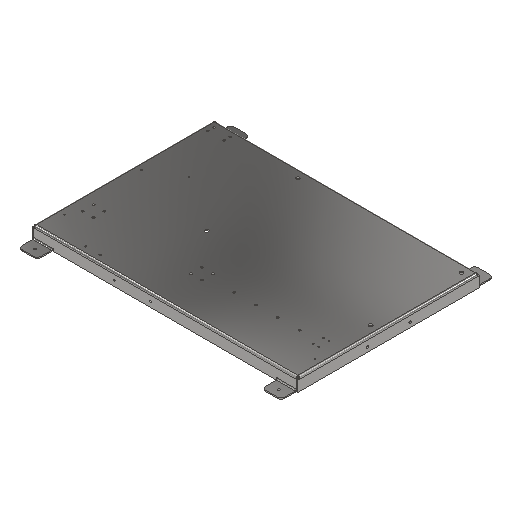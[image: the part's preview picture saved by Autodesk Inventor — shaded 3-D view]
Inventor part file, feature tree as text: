
AUTODESK INVENTOR PART (.ipt)
format: ipt  version: 2024.3 (Build 283343000, 343)  size: 646,656 bytes
history: native  units: mm
features: sketch x16, hole x13, sheet_metal_op x11, other x4, projected_geometry x3, mirror x2, fillet x1
ambient origin geometry x8: Origin, YZ Plane, XZ Plane, XY Plane, X Axis, Y Axis, Z Axis, Center Point
bodies: Solid1 (feature_tree)
feature tree (50):
  sheet_metal_op  "Face1"
  sheet_metal_op  "Flange1"
  sheet_metal_op  "Flange3"
  hole  "Hole1"  [1 undecoded]
  fillet  "Fillet1"  Radius=3.0mm
  mirror  "Mirror1"
  mirror  "Mirror2"
  hole  "Hole2"  [1 undecoded]
  hole  "Hole3"  [1 undecoded]
  hole  "Hole4"  [1 undecoded]
  hole  "Hole5"  [1 undecoded]
  hole  "Hole7"  [1 undecoded]
  hole  "Hole8"  [1 undecoded]
  hole  "Hole9"  [1 undecoded]
  hole  "Hole10"  [1 undecoded]
  hole  "Hole11"  [1 undecoded]
  hole  "Hole12"  [1 undecoded]
  hole  "Hole13"  [1 undecoded]
  hole  "Hole14"  [1 undecoded]
  sketch  "Sketch1"  dims[d0=730.0mm d1=500.0mm d2=3.0mm]
  other  "Plate1"
  sketch  "Sketch2"  dims[d3=3.0mm d4=1.5mm]
  other  "Plate2"
  sheet_metal_op  "Bend1"
  sheet_metal_op  "Corner1"
  sketch  "Sketch4"  dims[d5=6.0mm d6=3.0mm]
  other  "Plate4"
  sheet_metal_op  "Bend3"
  sheet_metal_op  "Corner7"
  sketch  "Sketch5"  dims[d7=35.0mm d8=90.0deg d9=3.0mm d10=12.0mm]
  projected_geometry  "Projected Loop1"
  sketch  "Sketch6"  dims[d11=3.0mm d12=3.0mm]
  sketch  "Sketch7"  dims[d13=12.0mm d14=3.0mm]
  sketch  "Sketch8"  dims[d15=1.0mm d16=0.0mm d17=10.0mm d18=12.0mm]
  sketch  "Sketch9"  dims[d19=3.0mm d20=1.0mm d21=0.0mm]
  projected_geometry  "Projected Loop2"
  projected_geometry  "Projected Loop3"
  sketch  "Sketch11"  dims[d22=10.0mm d23=12.0mm d24=3.0mm]
  sketch  "Sketch12"  dims[d25=1.0mm d26=0.0mm d27=10.0mm d28=12.0mm]
  sketch  "Sketch14"  dims[d29=3.0mm d30=1.0mm d31=0.0mm]
  sketch  "Sketch15"  dims[d32=10.0mm d43=3.0mm]
  sketch  "Sketch17"  dims[d44=1.5mm d45=6.0mm]
  sketch  "Sketch18"  dims[d46=3.0mm]
  sketch  "Sketch19"  dims[d47=0.0mm d48=670.0mm]
  sketch  "Sketch20"  dims[d49=45.0mm d50=90.0deg d51=3.0mm d52=12.0mm d53=3.0mm d54=3.0mm d55=6.6mm d56=6.0mm d57=18.0mm d58=4.8mm d59=90.0deg d60=3.0mm d61=20.594885mm d62=10.0mm d63=60.0mm d64=60.0mm d65=60.0mm d66=250.0mm d67=20.0mm d68=30.0mm d69=35.0mm d70=70.0mm d71=110.0mm d72=6.6mm d73=6.0mm d74=18.0mm d75=4.8mm d76=90.0deg d77=3.0mm d78=20.594885mm d79=30.0mm d80=30.0mm d81=37.5mm d82=101.0mm d83=6.6mm d84=6.0mm d85=4.0mm d86=2.0mm d87=90.0deg d88=8.0mm d89=20.594885mm d90=21.0mm d91=68.0mm d92=688.0mm d93=3.4mm d94=6.0mm d95=6.0mm d96=0.5mm d97=90.0deg d98=3.0mm d99=20.594885mm d100=15.0mm d101=28.1mm d102=45.0mm d103=102.5mm d104=4.5mm d105=6.0mm d106=8.0mm d107=4.6mm d108=90.0deg d109=8.0mm d110=20.594885mm d118=30.0mm d119=30.0mm d120=101.0mm d121=335.5mm d122=6.6mm d123=6.0mm d124=12.6mm d125=2.0mm d126=90.0deg d127=8.0mm d128=20.594885mm d129=450.0mm d130=250.0mm d131=25.0mm d132=25.0mm d133=10.0mm d134=6.0mm d135=17.3mm d136=2.0mm d137=90.0deg d138=3.0mm d139=0.0mm d142=20.0mm d143=280.0mm d144=48.4mm d145=82.5mm d146=4.5mm d147=6.0mm d148=9.4mm d149=2.0mm d150=90.0deg d151=8.0mm d152=0.0mm d153=45.0mm d154=16.5mm d155=19.5mm d156=18.5mm d157=5.8mm d158=6.0mm d159=10.4mm d160=2.0mm d161=90.0deg d162=8.0mm d163=0.0mm d164=100.0mm d165=225.0mm d166=14.5mm d167=5.5mm d168=6.0mm d169=10.4mm d170=2.0mm d171=90.0deg d172=8.0mm d173=0.0mm d174=117.0mm d175=13.0mm d176=6.6mm d177=6.0mm d178=12.6mm d179=2.0mm d180=90.0deg d181=8.0mm d182=0.0mm d183=3.4mm d184=6.0mm d185=4.0mm d186=2.0mm d187=90.0deg d188=8.0mm d189=0.0mm d190=4.5mm d191=6.0mm d192=4.0mm d193=2.0mm d194=90.0deg d195=8.0mm d196=0.0mm]
  sheet_metal_op  "Corner2"
  sheet_metal_op  "Corner3"
  sheet_metal_op  "Corner4"
  sheet_metal_op  "Corner5"
  other  "Definition1"
note: 13 required parameter values undecoded (feature->parameter linkage not recoverable at this tier; creation-order binding heuristic only, values carry confidence <= 0.55)
